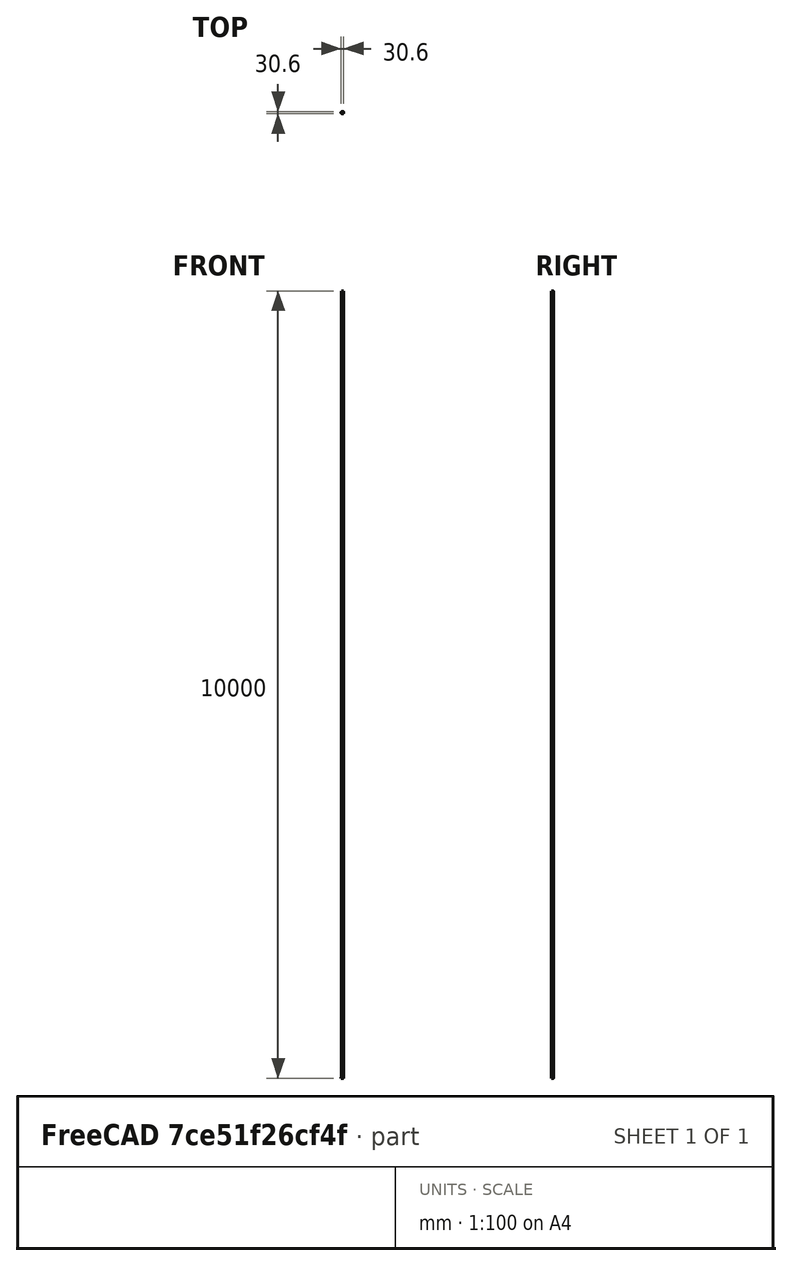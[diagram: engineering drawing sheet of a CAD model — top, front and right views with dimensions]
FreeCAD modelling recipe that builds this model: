
FCSTD DOCUMENT  (FreeCAD 0.16R)
Label: 25.4-28.6
License: All rights reserved
LicenseURL: http://en.wikipedia.org/wiki/All_rights_reserved
objects: Sketcher::SketchObject×4, PartDesign::Pad×2, PartDesign::Pocket×2, PartDesign::Chamfer×1, Mesh::Feature×1
note: 13 computed .brp shape members not serialized (recipe doc carries the construction recipe); baked Part::Feature solids carry a one-line shape summary decoded from their .brp

FEATURE [Sketcher::SketchObject] Sketch
  sketch-geometry (1):
    g0: Circle CenterX=0 CenterY=0 CenterZ=0 NormalX=0 NormalY=0 NormalZ=1 Radius=14.3
  constraints (1):
    c: Radius(g0) = 14.3
FEATURE [PartDesign::Pad] Pad
  Length = 10
  Length2 = 100
  Sketch = -> Sketch
  Type = 0
FEATURE [Sketcher::SketchObject] Sketch001
  Placement = pos=(0,0,10) rot=(0,0,1;0rad)
  Support = -> Pad [Face3]
  sketch-geometry (1):
    g0: Circle CenterX=0 CenterY=0 CenterZ=0 NormalX=0 NormalY=0 NormalZ=1 Radius=15.3
  constraints (2):
    c: Coincident(g0,g-1)
    c: Radius(g0) = 15.3
FEATURE [PartDesign::Pad] Pad001
  Length = 1.2
  Length2 = 100
  Sketch = -> Sketch001
  Type = 0
FEATURE [Sketcher::SketchObject] Sketch002
  Placement = pos=(0,0,0) rot=(1,0,0;3.14159rad)
  Support = -> Pad001 [Face1]
  sketch-geometry (1):
    g0: Circle CenterX=0 CenterY=0 CenterZ=0 NormalX=0 NormalY=0 NormalZ=1 Radius=12.7
  constraints (2):
    c: Coincident(g0,g-1)
    c: Radius(g0) = 12.7
FEATURE [PartDesign::Pocket] Pocket
  Length = 5
  Sketch = -> Sketch002
  Type = 1
FEATURE [Sketcher::SketchObject] Sketch003
  Placement = pos=(0,0,0) rot=(1,0,0;3.14159rad)
  Support = -> Pocket [Face1]
  sketch-geometry (4):
    g0: LineSegment StartX=-1 StartY=0 StartZ=0 EndX=1 EndY=0 EndZ=0
    g1: LineSegment StartX=1 StartY=0 StartZ=0 EndX=1 EndY=-19.9166 EndZ=0
    g2: LineSegment StartX=1 StartY=-19.9166 StartZ=0 EndX=-1 EndY=-19.9166 EndZ=0
    g3: LineSegment StartX=-1 StartY=-19.9166 StartZ=0 EndX=-1 EndY=0 EndZ=0
  constraints (12):
    c: Coincident(g0,g1)
    c: Coincident(g1,g2)
    c: Coincident(g2,g3)
    c: Coincident(g3,g0)
    c: Horizontal(g0)
    c: Horizontal(g2)
    c: Vertical(g1)
    c: Vertical(g3)
    c: Symmetric(g0,g0,g-2)
    c: PointOnObject(g0,g-1)
    c: Distance(g2) = 2
    c: Distance(g1) = 19.9166
FEATURE [PartDesign::Pocket] Pocket001
  Length = 5
  Sketch = -> Sketch003
  Type = 1
FEATURE [PartDesign::Chamfer] Chamfer
  Base = -> Pocket001 [Edge1,Edge2,Edge3,Edge4,Edge5,Edge6,Edge18,Edge19,Edge20,Edge21,Edge17,Edge10,Edge11,Edge12,Edge13,Edge9]
  Size = 0.3
FEATURE [Mesh::Feature] Mesh  label="Chamfer (Meshed)"
